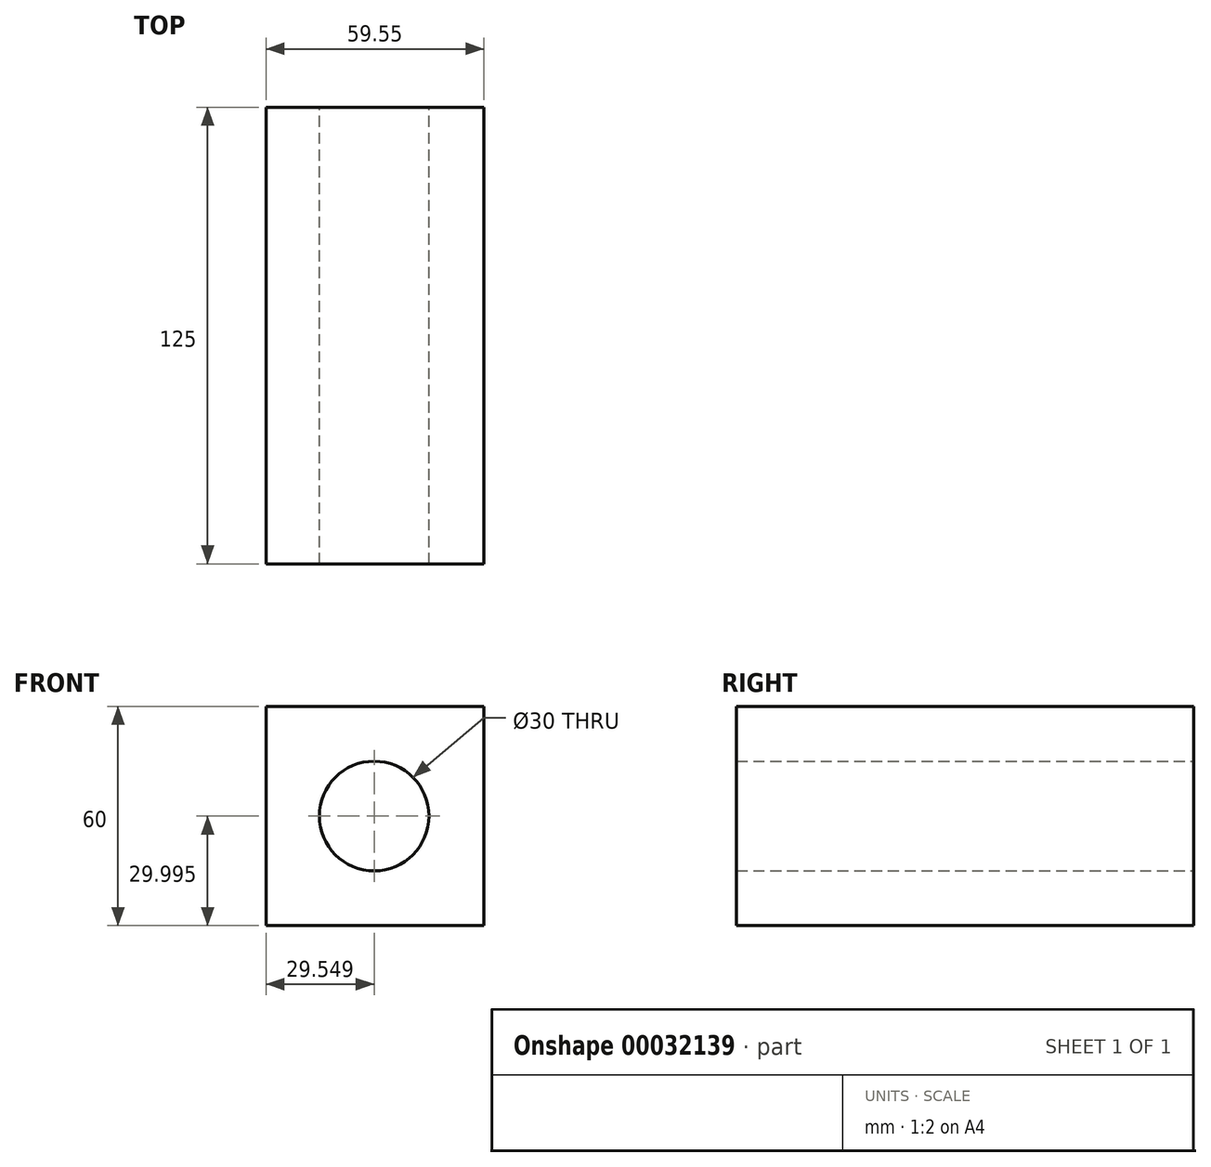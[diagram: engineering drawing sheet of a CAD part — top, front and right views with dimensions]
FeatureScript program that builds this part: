
annotation { "Feature Type Name" : "Feature", "Feature Type Description" : "" }
export const myFeature = defineFeature(function(context is Context, id is Id, definition is map)
    precondition{}
    {
        {
            var Q0;
            Q0=qCreatedBy(makeId("Front.planeOp"),FACE);
            var sketch = newSketch(context, id + "F0", { "sketchPlane" : qUnion([Q0])});
            skLineSegment(sketch, "E0.bottom", {"start": v(-0.45, -13.03) * mm, "end": v(-60, -13.03) * mm});
            skLineSegment(sketch, "E0.top", {"start": v(-0.45, 46.97) * mm, "end": v(-60, 46.97) * mm});
            skLineSegment(sketch, "E0.left", {"start": v(-0.45, -13.03) * mm, "end": v(-0.45, 46.97) * mm});
            skLineSegment(sketch, "E0.right", {"start": v(-60, -13.03) * mm, "end": v(-60, 46.97) * mm});
            skCircle(sketch, "E1", {"center": v(-30.45, 16.97) * mm, "radius": 15 * mm});
            skSolve(sketch);
        }
        {
            var Q0;
            Q0=makeQuery(id+"F0.imprint","IMPRINT",FACE,{"disambiguationData":[TD([[makeQuery(id+"F0.imprint","IMPRINT",EDGE,{"derivedFrom":sQuery(id+"F0.wireOp",EDGE,"E0.bottom")}),-1.0]])]});
            var Q1;
            Q1=makeQuery(id+"F0.imprint","IMPRINT",FACE,{"disambiguationData":[TD([[makeQuery(id+"F0.imprint","IMPRINT",EDGE,{"derivedFrom":sQuery(id+"F0.wireOp",EDGE,"E1")}),1.0]])]});
            extrude(context, id + "F1", {"entities" : qUnion([Q0, Q1]), "depth" : 125 * mm});
        }
        {
            var Q0;
            Q0=makeQuery(id+"F1.opExtrude","CAP_FACE",FACE,{"disambiguationData":[OSD([sQuery(id+"F0.wireOp",EDGE,"E0.bottom"),sQuery(id+"F0.wireOp",EDGE,"E0.top"),sQuery(id+"F0.wireOp",EDGE,"E0.left"),sQuery(id+"F0.wireOp",EDGE,"E0.right")])],"isStart":true});
            var sketch = newSketch(context, id + "F2", { "sketchPlane" : qUnion([Q0])});
            skCircle(sketch, "E2", {"center": v(30.45, 16.97) * mm, "radius": 15 * mm});
            skSolve(sketch);
        }
        {
            var Q0;
            Q0=makeQuery(id+"F2.imprint","IMPRINT",FACE,{"disambiguationData":[TD([[makeQuery(id+"F2.imprint","IMPRINT",EDGE,{"derivedFrom":sQuery(id+"F2.wireOp",EDGE,"E2")}),1.0]])]});
            var Q1;
            Q1=makeQuery(id+"F1.opExtrude","CAP_FACE",FACE,{"disambiguationData":[OSD([sQuery(id+"F0.wireOp",EDGE,"E0.bottom"),sQuery(id+"F0.wireOp",EDGE,"E0.top"),sQuery(id+"F0.wireOp",EDGE,"E0.left"),sQuery(id+"F0.wireOp",EDGE,"E0.right")])],"isStart":false});
            extrude(context, id + "F3", {"entities" : qUnion([Q0, Q1]), "operationType" : NewBodyOperationType.REMOVE, "endBound" : BoundingType.THROUGH_ALL, "oppositeDirection" : true, "depth" : 25 * mm});
        }
    });
